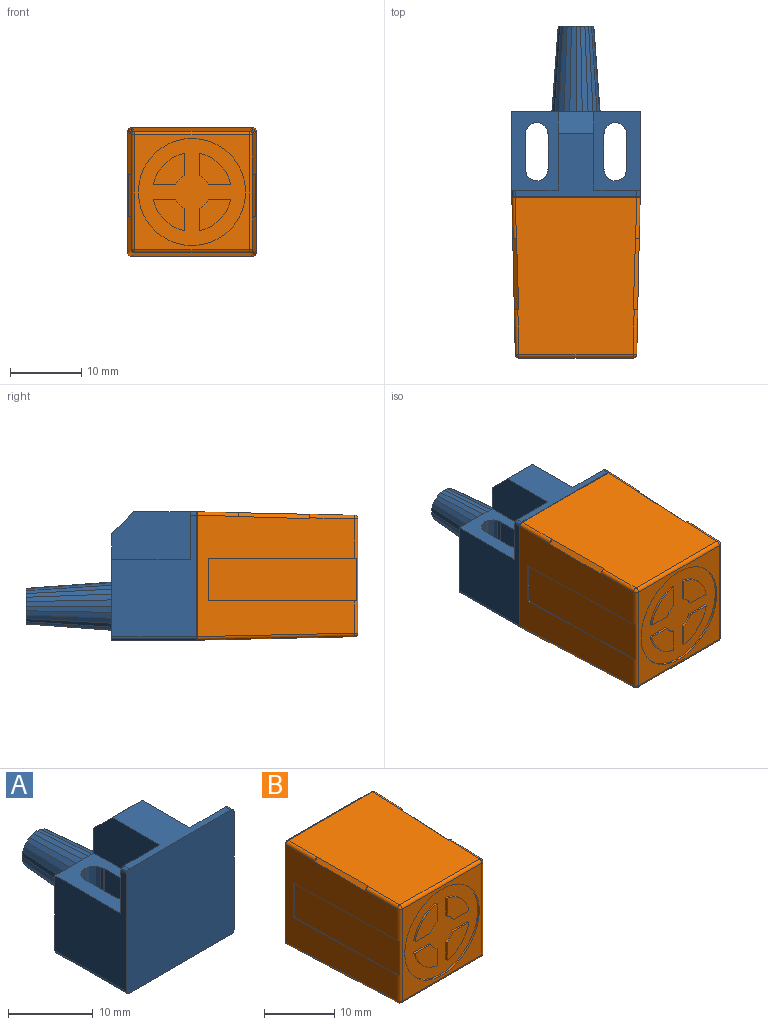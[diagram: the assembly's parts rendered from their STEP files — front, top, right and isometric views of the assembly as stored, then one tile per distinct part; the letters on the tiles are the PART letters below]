
ASSEMBLY  parts=2 mates=1
PART A: 88 faces, bbox 18x23.9x18 mm
  f0: plane 18x18mm, normal (0,-1,0), area 323.8mm2, adj f80,f81,f82,f83,f84,f85,f86,f87
  f1: plane 5x5mm, normal (0,1,0), area 19.4mm2, adj f2,f3,f4,f5,f6,f7,f8,f9
  f2: plane 12x0.96mm, normal (-0.99,0.07,0.13), area 9.2mm2, adj f1,f3,f25,f78
  f3: plane 12x1.1mm, normal (-0.92,0.07,0.38), area 9.2mm2, adj f1,f2,f4,f78
  f4: plane 12x1.16mm, normal (-0.79,0.07,0.61), area 9.2mm2, adj f1,f3,f5,f78
  f5: plane 12x1.16mm, normal (-0.61,0.07,0.79), area 9.2mm2, adj f1,f4,f6,f78
  f6: plane 12x1.1mm, normal (-0.38,0.07,0.92), area 9.2mm2, adj f1,f5,f7,f78
  f7: plane 12x0.96mm, normal (-0.13,0.07,0.99), area 9.2mm2, adj f1,f6,f8,f78
  f8: plane 12x0.96mm, normal (0.13,0.07,0.99), area 9.2mm2, adj f1,f7,f9,f78
  f9: plane 12x1.1mm, normal (0.38,0.07,0.92), area 9.2mm2, adj f1,f8,f10,f78
  f10: plane 12x1.16mm, normal (0.61,0.07,0.79), area 9.2mm2, adj f1,f9,f11,f78
  f11: plane 12x1.16mm, normal (0.79,0.07,0.61), area 9.2mm2, adj f1,f10,f12,f78
  f12: plane 12x1.1mm, normal (0.92,0.07,0.38), area 9.2mm2, adj f1,f11,f13,f78
  f13: plane 12x0.96mm, normal (0.99,0.07,0.13), area 9.2mm2, adj f1,f12,f14,f78
  f14: plane 12x0.96mm, normal (0.99,0.07,-0.13), area 9.2mm2, adj f1,f13,f15,f78
  f15: plane 12x1.1mm, normal (0.92,0.07,-0.38), area 9.2mm2, adj f1,f14,f16,f78
  f16: plane 12x1.16mm, normal (0.79,0.07,-0.61), area 9.2mm2, adj f1,f15,f17,f78
  f17: plane 12x1.16mm, normal (0.61,0.07,-0.79), area 9.2mm2, adj f1,f16,f18,f78
  f18: plane 12x1.1mm, normal (0.38,0.07,-0.92), area 9.2mm2, adj f1,f17,f19,f78
  f19: plane 12x0.96mm, normal (0.13,0.07,-0.99), area 9.2mm2, adj f1,f18,f20,f78
  f20: plane 12x0.96mm, normal (-0.13,0.07,-0.99), area 9.2mm2, adj f1,f19,f21,f78
  f21: plane 12x1.1mm, normal (-0.38,0.07,-0.92), area 9.2mm2, adj f1,f20,f22,f78
  f22: plane 12x1.16mm, normal (-0.61,0.07,-0.79), area 9.2mm2, adj f1,f21,f23,f78
  f23: plane 12x1.16mm, normal (-0.79,0.07,-0.61), area 9.2mm2, adj f1,f22,f24,f78
  f24: plane 12x1.1mm, normal (-0.92,0.07,-0.38), area 9.2mm2, adj f1,f23,f25,f78
  f25: plane 12x0.96mm, normal (-0.99,0.07,-0.13), area 9.2mm2, adj f1,f2,f24,f78
  f26: plane 11.33x0.63mm, normal (0.95,0.31,0), area 7.5mm2, adj f27,f48,f73,f87
  f27: plane 11.33x0.17mm, normal (0.99,-0.1,0), area 1.9mm2, adj f26,f28,f73,f87
  f28: plane 11.33x0.03mm, normal (0,1,0), area 0.3mm2, adj f27,f29,f73,f87
  f29: plane 11.33x5mm, normal (1,0,0), area 56.7mm2, adj f28,f30,f73,f87
  f30: plane 11.33x0.03mm, normal (0,-1,0), area 0.3mm2, adj f29,f31,f73,f87
  f31: plane 11.33x0.49mm, normal (0.99,-0.1,0), area 5.6mm2, adj f30,f32,f73,f87
  f32: plane 11.33x0.58mm, normal (0.87,-0.5,0), area 7.5mm2, adj f31,f33,f73,f87
  f33: plane 11.33x0.54mm, normal (0.59,-0.81,0), area 7.5mm2, adj f32,f34,f73,f87
  f34: plane 11.33x0.65mm, normal (0.21,-0.98,0), area 7.5mm2, adj f33,f35,f73,f87
  f35: plane 11.33x0.65mm, normal (-0.21,-0.98,0), area 7.5mm2, adj f34,f36,f73,f87
  f36: plane 11.33x0.54mm, normal (-0.59,-0.81,0), area 7.5mm2, adj f35,f37,f73,f87
  f37: plane 11.33x0.58mm, normal (-0.87,-0.5,0), area 7.5mm2, adj f36,f38,f73,f87
  f38: plane 11.33x0.49mm, normal (-0.99,-0.1,0), area 5.6mm2, adj f37,f39,f73,f87
  f39: plane 11.33x0.03mm, normal (0,-1,0), area 0.3mm2, adj f38,f40,f73,f87
  f40: plane 11.33x5mm, normal (-1,0,0), area 56.7mm2, adj f39,f41,f73,f87
  f41: plane 11.33x0.03mm, normal (0,1,0), area 0.3mm2, adj f40,f42,f73,f87
  f42: plane 11.33x0.17mm, normal (-0.99,-0.1,0), area 1.9mm2, adj f41,f43,f73,f87
  f43: plane 11.33x0.63mm, normal (-0.95,0.31,0), area 7.5mm2, adj f42,f44,f73,f87
  f44: plane 11.33x0.49mm, normal (-0.74,0.67,0), area 7.5mm2, adj f43,f45,f73,f87
  f45: plane 11.33x0.61mm, normal (-0.41,0.91,0), area 7.5mm2, adj f44,f46,f73,f87
  f46: plane 11.33x0.67mm, normal (0,1,0), area 7.5mm2, adj f45,f47,f73,f87
  f47: plane 11.33x0.61mm, normal (0.41,0.91,0), area 7.5mm2, adj f46,f48,f73,f87
  f48: plane 11.33x0.49mm, normal (0.74,0.67,0), area 7.5mm2, adj f26,f47,f73,f87
  f49: plane 11.33x0.65mm, normal (-0.21,-0.98,0), area 7.5mm2, adj f50,f71,f72,f87
  f50: plane 11.33x0.54mm, normal (-0.59,-0.81,0), area 7.5mm2, adj f49,f51,f72,f87
  f51: plane 11.33x0.58mm, normal (-0.87,-0.5,0), area 7.5mm2, adj f50,f52,f72,f87
  f52: plane 11.33x0.49mm, normal (-0.99,-0.1,0), area 5.6mm2, adj f51,f53,f72,f87
  f53: plane 11.33x0.03mm, normal (0,-1,0), area 0.3mm2, adj f52,f54,f72,f87
  f54: plane 11.33x5mm, normal (-1,0,0), area 56.7mm2, adj f53,f55,f72,f87
  f55: plane 11.33x0.03mm, normal (0,1,0), area 0.3mm2, adj f54,f56,f72,f87
  f56: plane 11.33x0.17mm, normal (-0.99,-0.1,0), area 1.9mm2, adj f55,f57,f72,f87
  f57: plane 11.33x0.63mm, normal (-0.95,0.31,0), area 7.5mm2, adj f56,f58,f72,f87
  f58: plane 11.33x0.49mm, normal (-0.74,0.67,0), area 7.5mm2, adj f57,f59,f72,f87
  f59: plane 11.33x0.61mm, normal (-0.41,0.91,0), area 7.5mm2, adj f58,f60,f72,f87
  f60: plane 11.33x0.67mm, normal (0,1,0), area 7.5mm2, adj f59,f61,f72,f87
  f61: plane 11.33x0.61mm, normal (0.41,0.91,0), area 7.5mm2, adj f60,f62,f72,f87
  f62: plane 11.33x0.49mm, normal (0.74,0.67,0), area 7.5mm2, adj f61,f63,f72,f87
  f63: plane 11.33x0.63mm, normal (0.95,0.31,0), area 7.5mm2, adj f62,f64,f72,f87
  f64: plane 11.33x0.17mm, normal (0.99,-0.1,0), area 1.9mm2, adj f63,f65,f72,f87
  f65: plane 11.33x0.03mm, normal (0,1,0), area 0.3mm2, adj f64,f66,f72,f87
  f66: plane 11.33x5mm, normal (1,0,0), area 56.7mm2, adj f65,f67,f72,f87
  f67: plane 11.33x0.03mm, normal (0,-1,0), area 0.3mm2, adj f66,f68,f72,f87
  f68: plane 11.33x0.49mm, normal (0.99,-0.1,0), area 5.6mm2, adj f67,f69,f72,f87
  f69: plane 11.33x0.58mm, normal (0.87,-0.5,0), area 7.5mm2, adj f68,f70,f72,f87
  f70: plane 11.33x0.54mm, normal (0.59,-0.81,0), area 7.5mm2, adj f69,f71,f72,f87
  f71: plane 11.33x0.65mm, normal (0.21,-0.98,0), area 7.5mm2, adj f49,f70,f72,f87
  f72: plane 11x6.5mm, normal (0,0,1), area 47.7mm2, adj f49,f50,f51,f52,f53,f54,f55,f56
  f73: plane 11x6.5mm, normal (0,0,1), area 47.7mm2, adj f26,f27,f28,f29,f30,f31,f32,f33
  f74: plane 11x6.67mm, normal (-1,0,0), area 68.6mm2, adj f72,f75,f77,f78,f83
  f75: plane 5x3.07mm, normal (0,0.71,0.71), area 21.7mm2, adj f74,f76,f78,f83
  f76: plane 11x6.67mm, normal (1,0,0), area 68.6mm2, adj f73,f75,f78,f79,f83
  f77: plane 6.67x6.5mm, normal (0,1,0), area 43.3mm2, adj f72,f74,f81,f83,f86
  f78: plane 18x14.93mm, normal (0,1,0), area 186.5mm2, adj f2,f3,f4,f5,f6,f7,f8,f9
  f79: plane 6.67x6.5mm, normal (0,1,0), area 43.3mm2, adj f73,f76,f82,f83,f85
  f80: cylinder r=0.5mm len=11.9mm, axis (0,1,0), area 9.3mm2, adj f0,f78,f86,f87
  f81: cylinder r=0.5mm len=0.9mm, axis (0,1,0), area 0.7mm2, adj f0,f77,f83,f86
  f82: cylinder r=0.5mm len=0.9mm, axis (0,1,0), area 0.7mm2, adj f0,f79,f83,f85
  f83: plane 17x8.83mm, normal (0,0,1), area 54.9mm2, adj f0,f74,f75,f76,f77,f79,f81,f82
  f84: cylinder r=0.5mm len=11.9mm, axis (0,1,0), area 9.3mm2, adj f0,f78,f85,f87
  f85: plane 17x11.9mm, normal (1,0,0), area 134.5mm2, adj f0,f73,f78,f79,f82,f84
  f86: plane 17x11.9mm, normal (-1,0,0), area 134.5mm2, adj f0,f72,f77,f78,f80,f81
  f87: plane 17x11.9mm, normal (0,0,-1), area 154.7mm2, adj f0,f26,f27,f28,f29,f30,f31,f32
PART B: 65 faces, bbox 18x22.6x18 mm
  f0: plane 17x0.1mm, normal (0,0,-1), area 1.7mm2, adj f4,f58,f62,f64
  f1: plane 17x0.1mm, normal (-1,0,0), area 1.7mm2, adj f4,f58,f59,f64
  f2: plane 17x0.1mm, normal (1,0,0), area 1.7mm2, adj f4,f62,f63,f64
  f3: plane 17x0.1mm, normal (0,0,1), area 1.7mm2, adj f4,f59,f63,f64
  f4: plane 18.01x18.01mm, normal (0,-1,0), area 0.8mm2, adj f0,f1,f2,f3,f5,f6,f7,f8
  f5: plane 22.01x16.98mm, normal (0,-0.02,-1), area 363.3mm2, adj f4,f46,f51,f52
  f6: plane 22.01x16.98mm, normal (1,-0.02,0), area 239.4mm2, adj f4,f10,f11,f12,f13,f14,f15,f51
  f7: plane 22.01x16.98mm, normal (0,-0.02,1), area 361.8mm2, adj f4,f10,f11,f12,f16,f17,f18,f48
  f8: plane 22.01x16.98mm, normal (-1,-0.02,0), area 239.4mm2, adj f4,f16,f17,f18,f19,f20,f21,f46
  f9: plane 16.02x16.02mm, normal (0,-1,0), area 80mm2, adj f24,f47,f52,f53,f57
  f10: plane 0.62x0.62mm, normal (0,1,0.05), area 0.1mm2, adj f6,f7,f11,f54
  f11: plane 10.03x0.84mm, normal (0.71,-0.04,0.71), area 8.1mm2, adj f6,f7,f10,f12
  f12: plane 0.53x0.53mm, normal (0,-1,-0.05), area 0.1mm2, adj f6,f7,f11,f61
  f13: plane 20.78x0.53mm, normal (0,0,1), area 2.5mm2, adj f6,f14,f23,f57
  f14: plane 6x0.16mm, normal (-0.02,-1,0), area 1mm2, adj f6,f13,f15,f23
  f15: plane 20.78x0.53mm, normal (0,0,-1), area 2.5mm2, adj f6,f14,f23,f57
  f16: plane 0.62x0.62mm, normal (0,1,0.05), area 0.1mm2, adj f7,f8,f17,f48
  f17: plane 10.03x0.84mm, normal (-0.71,-0.04,0.71), area 8.1mm2, adj f7,f8,f16,f18
  f18: plane 0.53x0.53mm, normal (0,-1,-0.05), area 0.1mm2, adj f7,f8,f17,f60
  f19: plane 20.78x0.53mm, normal (0,0,-1), area 2.5mm2, adj f8,f20,f22,f47
  f20: plane 6x0.16mm, normal (0.02,-1,0), area 1mm2, adj f8,f19,f21,f22
  f21: plane 20.78x0.53mm, normal (0,0,1), area 2.5mm2, adj f8,f20,f22,f47
  f22: plane 20.78x6mm, normal (-1,-0.02,0), area 124.7mm2, adj f19,f20,f21,f47
  f23: plane 20.78x6mm, normal (1,-0.02,0), area 124.7mm2, adj f13,f14,f15,f57
  f24: cylinder r=7.5mm len=15mm, axis (0,1,0), area 14.1mm2, adj f9,f25
  f25: plane 15x15mm, normal (0,-1,0), area 125.6mm2, adj f24,f26,f27,f28,f29,f30,f31,f32
  f26: plane 3.12x0.3mm, normal (0,0,-1), area 0.9mm2, adj f25,f27,f29,f42
  f27: cylinder r=2.5mm len=1.29mm, axis (0,1,0), area 0.6mm2, adj f25,f26,f28,f42
  f28: plane 3.12x0.3mm, normal (1,0,0), area 0.9mm2, adj f25,f27,f29,f42
  f29: cylinder r=5.5mm len=4.41mm, axis (0,1,0), area 2mm2, adj f25,f26,f28,f42
  f30: plane 3.12x0.3mm, normal (1,0,0), area 0.9mm2, adj f25,f31,f33,f43
  f31: cylinder r=2.5mm len=1.29mm, axis (0,1,0), area 0.6mm2, adj f25,f30,f32,f43
  f32: plane 3.12x0.3mm, normal (0,0,1), area 0.9mm2, adj f25,f31,f33,f43
  f33: cylinder r=5.5mm len=4.41mm, axis (0,1,0), area 2mm2, adj f25,f30,f32,f43
  f34: plane 3.12x0.3mm, normal (0,0,1), area 0.9mm2, adj f25,f35,f37,f44
  f35: cylinder r=2.5mm len=1.29mm, axis (0,1,0), area 0.6mm2, adj f25,f34,f36,f44
  f36: plane 3.12x0.3mm, normal (-1,0,0), area 0.9mm2, adj f25,f35,f37,f44
  f37: cylinder r=5.5mm len=4.41mm, axis (0,1,0), area 2mm2, adj f25,f34,f36,f44
  f38: plane 3.12x0.3mm, normal (-1,0,0), area 0.9mm2, adj f25,f39,f41,f45
  f39: cylinder r=2.5mm len=1.29mm, axis (0,1,0), area 0.6mm2, adj f25,f38,f40,f45
  f40: plane 3.12x0.3mm, normal (0,0,-1), area 0.9mm2, adj f25,f39,f41,f45
  f41: cylinder r=5.5mm len=4.41mm, axis (0,1,0), area 2mm2, adj f25,f38,f40,f45
  f42: plane 4.41x4.41mm, normal (0,-1,0), area 12.8mm2, adj f26,f27,f28,f29
  f43: plane 4.41x4.41mm, normal (0,-1,0), area 12.8mm2, adj f30,f31,f32,f33
  f44: plane 4.41x4.41mm, normal (0,-1,0), area 12.8mm2, adj f34,f35,f36,f37
  f45: plane 4.41x4.41mm, normal (0,-1,0), area 12.8mm2, adj f38,f39,f40,f41
  f46: cylinder r=0.5mm len=22.02mm, axis (-0.02,1,-0.02), area 17.3mm2, adj f4,f5,f8,f49
  f47: cylinder r=0.5mm len=16.02mm, axis (0,0,1), area 10.7mm2, adj f8,f9,f19,f21,f22,f49,f50
  f48: cylinder r=0.5mm len=6.26mm, axis (-0.02,1,0.02), area 4.9mm2, adj f7,f8,f16,f50
  f49: sphere r=0.5mm, area 0.4mm2, adj f46,f47,f52
  f50: sphere r=0.5mm, area 0.4mm2, adj f47,f48,f53
  f51: cylinder r=0.5mm len=22.02mm, axis (0.02,1,-0.02), area 17.3mm2, adj f4,f5,f6,f55
  f52: cylinder r=0.5mm len=16.02mm, axis (-1,0,0), area 12.4mm2, adj f5,f9,f49,f55
  f53: cylinder r=0.5mm len=16.02mm, axis (1,0,0), area 12.4mm2, adj f7,f9,f50,f56
  f54: cylinder r=0.5mm len=6.26mm, axis (0.02,1,0.02), area 4.9mm2, adj f6,f7,f10,f56
  f55: sphere r=0.5mm, area 0.4mm2, adj f51,f52,f57
  f56: sphere r=0.5mm, area 0.4mm2, adj f53,f54,f57
  f57: cylinder r=0.5mm len=16.02mm, axis (0,0,-1), area 10.7mm2, adj f6,f9,f13,f15,f23,f55,f56
  f58: cylinder r=0.5mm len=0.5mm, axis (0,1,0), area 0.1mm2, adj f0,f1,f4,f64
  f59: cylinder r=0.5mm len=0.5mm, axis (0,1,0), area 0.1mm2, adj f1,f3,f4,f64
  f60: cylinder r=0.5mm len=5.78mm, axis (-0.02,1,0.02), area 4.5mm2, adj f4,f7,f8,f18
  f61: cylinder r=0.5mm len=5.78mm, axis (0.02,1,0.02), area 4.5mm2, adj f4,f6,f7,f12
  f62: cylinder r=0.5mm len=0.5mm, axis (0,1,0), area 0.1mm2, adj f0,f2,f4,f64
  f63: cylinder r=0.5mm len=0.5mm, axis (0,1,0), area 0.1mm2, adj f2,f3,f4,f64
  f64: plane 18x18mm, normal (0,1,0), area 323.8mm2, adj f0,f1,f2,f3,f58,f59,f62,f63
PLACE A at identity
PLACE B at identity
MATE fastened B.f24 <-> A.f0  axis (0,1,0) through (0,-3.9,9)mm
